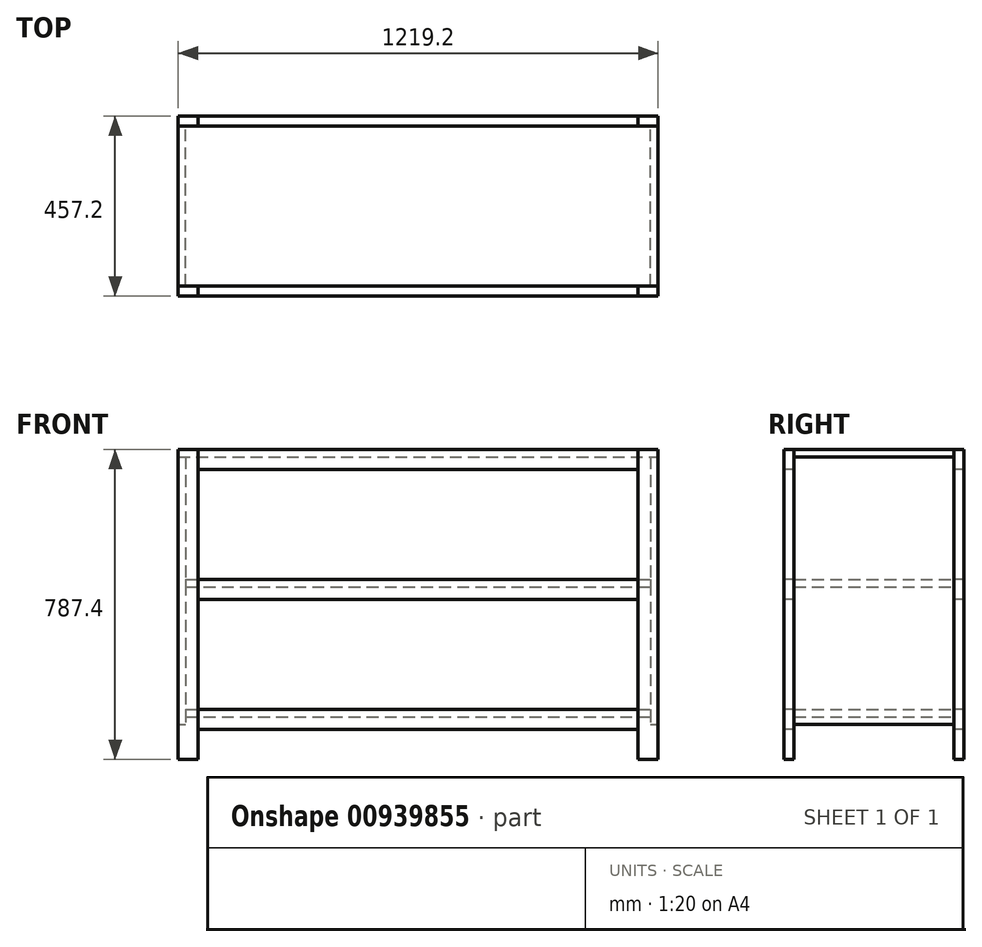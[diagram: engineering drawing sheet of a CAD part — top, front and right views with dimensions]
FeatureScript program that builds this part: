
annotation { "Feature Type Name" : "Feature", "Feature Type Description" : "" }
export const myFeature = defineFeature(function(context is Context, id is Id, definition is map)
    precondition{}
    {
        {
            var Q0;
            Q0=qCreatedBy(makeId("Front.planeOp"),FACE);
            var sketch = newSketch(context, id + "F0", { "sketchPlane" : qUnion([Q0])});
            skLineSegment(sketch, "E0", {"start": v(-1219.2, 0) * mm, "end": v(0, 0) * mm, "construction": true});
            skLineSegment(sketch, "E1", {"start": v(0, 787.4) * mm, "end": v(-1219.2, 787.4) * mm, "construction": true});
            skLineSegment(sketch, "E2", {"start": v(-1219.2, 787.4) * mm, "end": v(-1219.2, 0) * mm, "construction": true});
            skLineSegment(sketch, "E3", {"start": v(0, 0) * mm, "end": v(1219.2, 0) * mm, "construction": true});
            skLineSegment(sketch, "E4", {"start": v(1219.2, 0) * mm, "end": v(1219.2, 787.4) * mm, "construction": true});
            skLineSegment(sketch, "E5", {"start": v(1219.2, 787.4) * mm, "end": v(0, 787.4) * mm, "construction": true});
            skLineSegment(sketch, "E6", {"start": v(0, 787.4) * mm, "end": v(0, 0) * mm, "construction": true});
            skLineSegment(sketch, "E7.0", {"start": v(-19.05, 768.35) * mm, "end": v(-19.05, 88.9) * mm, "construction": true});
            skLineSegment(sketch, "E8.0", {"start": v(-1200.15, 768.35) * mm, "end": v(-1200.15, 88.9) * mm, "construction": true});
            skLineSegment(sketch, "E9.0", {"start": v(19.05, 787.4) * mm, "end": v(19.05, 0) * mm, "construction": true});
            skLineSegment(sketch, "E10.0", {"start": v(1200.15, 0) * mm, "end": v(1200.15, 787.4) * mm, "construction": true});
            skLineSegment(sketch, "E11.0", {"start": v(0, 768.35) * mm, "end": v(-1219.2, 768.35) * mm, "construction": true});
            skLineSegment(sketch, "E12.0", {"start": v(-19.05, 457.2) * mm, "end": v(-1200.15, 457.2) * mm, "construction": true});
            skLineSegment(sketch, "E13.0", {"start": v(-19.05, 438.15) * mm, "end": v(-1200.15, 438.15) * mm, "construction": true});
            skLineSegment(sketch, "E14.0", {"start": v(-19.05, 127) * mm, "end": v(-1200.15, 127) * mm, "construction": true});
            skLineSegment(sketch, "E15.0", {"start": v(-19.05, 107.95) * mm, "end": v(-1200.15, 107.95) * mm, "construction": true});
            skLineSegment(sketch, "E16.0", {"start": v(0, 88.9) * mm, "end": v(-19.05, 88.9) * mm, "construction": true});
            skLineSegment(sketch, "E17.trimOffspring", {"start": v(-1200.15, 88.9) * mm, "end": v(-1219.2, 88.9) * mm, "construction": true});
            skLineSegment(sketch, "E18.bottom", {"start": v(-1219.2, 787.4) * mm, "end": v(0, 787.4) * mm});
            skLineSegment(sketch, "E18.top", {"start": v(-1219.2, 768.35) * mm, "end": v(0, 768.35) * mm});
            skLineSegment(sketch, "E18.left", {"start": v(-1219.2, 787.4) * mm, "end": v(-1219.2, 768.35) * mm});
            skLineSegment(sketch, "E18.right", {"start": v(0, 787.4) * mm, "end": v(0, 768.35) * mm});
            skLineSegment(sketch, "E19.bottom", {"start": v(-1219.2, 768.35) * mm, "end": v(-1200.15, 768.35) * mm});
            skLineSegment(sketch, "E19.top", {"start": v(-1219.2, 88.9) * mm, "end": v(-1200.15, 88.9) * mm});
            skLineSegment(sketch, "E19.left", {"start": v(-1219.2, 768.35) * mm, "end": v(-1219.2, 88.9) * mm});
            skLineSegment(sketch, "E19.right", {"start": v(-1200.15, 768.35) * mm, "end": v(-1200.15, 88.9) * mm});
            skLineSegment(sketch, "E20.bottom", {"start": v(-19.05, 768.35) * mm, "end": v(0, 768.35) * mm});
            skLineSegment(sketch, "E20.top", {"start": v(-19.05, 88.9) * mm, "end": v(0, 88.9) * mm});
            skLineSegment(sketch, "E20.left", {"start": v(-19.05, 768.35) * mm, "end": v(-19.05, 88.9) * mm});
            skLineSegment(sketch, "E20.right", {"start": v(0, 768.35) * mm, "end": v(0, 88.9) * mm});
            skLineSegment(sketch, "E21.bottom", {"start": v(-1200.15, 457.2) * mm, "end": v(-19.05, 457.2) * mm});
            skLineSegment(sketch, "E21.top", {"start": v(-1200.15, 438.15) * mm, "end": v(-19.05, 438.15) * mm});
            skLineSegment(sketch, "E21.left", {"start": v(-1200.15, 457.2) * mm, "end": v(-1200.15, 438.15) * mm});
            skLineSegment(sketch, "E21.right", {"start": v(-19.05, 457.2) * mm, "end": v(-19.05, 438.15) * mm});
            skLineSegment(sketch, "E22.bottom", {"start": v(-1200.15, 127) * mm, "end": v(-19.05, 127) * mm});
            skLineSegment(sketch, "E22.top", {"start": v(-1200.15, 107.95) * mm, "end": v(-19.05, 107.95) * mm});
            skLineSegment(sketch, "E22.left", {"start": v(-1200.15, 127) * mm, "end": v(-1200.15, 107.95) * mm});
            skLineSegment(sketch, "E22.right", {"start": v(-19.05, 127) * mm, "end": v(-19.05, 107.95) * mm});
            skSolve(sketch);
        }
        {
            var Q0;
            Q0=makeQuery(id+"F0.imprint","IMPRINT",FACE,{"disambiguationData":[TD([[makeQuery(id+"F0.imprint","IMPRINT",EDGE,{"derivedFrom":sQuery(id+"F0.wireOp",EDGE,"E18.bottom")}),-1.0]])]});
            extrude(context, id + "F1", {"entities" : qUnion([Q0]), "depth" : 406.4 * mm, "offsetDistance" : 25.4 * mm});
        }
        {
            var Q0;
            {var subQ7=sQuery(id+"F0.wireOp",EDGE,"E20.top");Q0=makeQuery(id+"F0.imprint","IMPRINT",FACE,{"disambiguationData":[TD([[makeQuery(id+"F0.imprint","IMPRINT",EDGE,{"derivedFrom":subQ7}),1.0]])]});}
            extrude(context, id + "F2", {"entities" : qUnion([Q0]), "depth" : 406.4 * mm, "offsetDistance" : 25.4 * mm});
        }
        {
            var Q0;
            {var subQ3=sQuery(id+"F0.wireOp",EDGE,"E19.top");Q0=makeQuery(id+"F0.imprint","IMPRINT",FACE,{"disambiguationData":[TD([[makeQuery(id+"F0.imprint","IMPRINT",EDGE,{"derivedFrom":subQ3}),1.0]])]});}
            extrude(context, id + "F3", {"entities" : qUnion([Q0]), "depth" : 406.4 * mm, "offsetDistance" : 25.4 * mm});
        }
        {
            var Q0;
            {var subQ2=sQuery(id+"F0.wireOp",EDGE,"E21.bottom");Q0=makeQuery(id+"F0.imprint","IMPRINT",FACE,{"disambiguationData":[TD([[makeQuery(id+"F0.imprint","IMPRINT",EDGE,{"derivedFrom":subQ2}),-1.0]])]});}
            extrude(context, id + "F4", {"entities" : qUnion([Q0]), "depth" : 406.4 * mm, "offsetDistance" : 25.4 * mm});
        }
        {
            var Q0;
            {var subQ0=sQuery(id+"F0.wireOp",EDGE,"E22.bottom");Q0=makeQuery(id+"F0.imprint","IMPRINT",FACE,{"disambiguationData":[TD([[makeQuery(id+"F0.imprint","IMPRINT",EDGE,{"derivedFrom":subQ0}),-1.0]])]});}
            extrude(context, id + "F5", {"entities" : qUnion([Q0]), "depth" : 406.4 * mm, "offsetDistance" : 25.4 * mm});
        }
        {
            var Q0;
            Q0=makeQuery(id+"F1.opExtrude","SWEPT_FACE",FACE,{"disambiguationData":[OSD([sQuery(id+"F0.wireOp",EDGE,"E18.bottom")])]});
            var sketch = newSketch(context, id + "F6", { "sketchPlane" : qUnion([Q0])});
            skLineSegment(sketch, "E23.0", {"start": v(-1219.2, -431.8) * mm, "end": v(0, -431.8) * mm});
            skLineSegment(sketch, "E24.0", {"start": v(-1168.4, -406.4) * mm, "end": v(-1168.4, 0) * mm});
            skLineSegment(sketch, "E25.0", {"start": v(-50.8, -406.4) * mm, "end": v(-50.8, 0) * mm});
            skLineSegment(sketch, "E26.bottom", {"start": v(-50.8, -406.4) * mm, "end": v(0, -406.4) * mm});
            skLineSegment(sketch, "E26.top", {"start": v(-50.8, -431.8) * mm, "end": v(0, -431.8) * mm});
            skLineSegment(sketch, "E26.left", {"start": v(-50.8, -406.4) * mm, "end": v(-50.8, -431.8) * mm});
            skLineSegment(sketch, "E26.right", {"start": v(0, -406.4) * mm, "end": v(0, -431.8) * mm});
            skLineSegment(sketch, "E27.bottom", {"start": v(-1168.4, -406.4) * mm, "end": v(-1219.2, -406.4) * mm});
            skLineSegment(sketch, "E27.top", {"start": v(-1168.4, -431.8) * mm, "end": v(-1219.2, -431.8) * mm});
            skLineSegment(sketch, "E27.left", {"start": v(-1168.4, -406.4) * mm, "end": v(-1168.4, -431.8) * mm});
            skLineSegment(sketch, "E27.right", {"start": v(-1219.2, -406.4) * mm, "end": v(-1219.2, -431.8) * mm});
            skSolve(sketch);
        }
        {
            var Q0;
            Q0=makeQuery(id+"F6.imprint","IMPRINT",FACE,{"disambiguationData":[TD([[makeQuery(id+"F6.imprint","IMPRINT",EDGE,{"derivedFrom":sQuery(id+"F6.wireOp",EDGE,"E27.bottom")}),-1.0]])]});
            extrude(context, id + "F7", {"entities" : qUnion([Q0]), "oppositeDirection" : true, "depth" : 787.4 * mm, "offsetDistance" : 25.4 * mm});
        }
        {
            var Q0;
            Q0=makeQuery(id+"F6.imprint","IMPRINT",FACE,{"disambiguationData":[TD([[makeQuery(id+"F6.imprint","IMPRINT",EDGE,{"derivedFrom":sQuery(id+"F6.wireOp",EDGE,"E26.bottom")}),-1.0]])]});
            extrude(context, id + "F8", {"entities" : qUnion([Q0]), "oppositeDirection" : true, "depth" : 787.4 * mm, "offsetDistance" : 25.4 * mm});
        }
        {
            var Q0;
            {var subQ2=sQuery(id+"F6.wireOp",EDGE,"E26.left");Q0=makeQuery(id+"F6.imprint","IMPRINT",FACE,{"disambiguationData":[TD([[makeQuery(id+"F6.imprint","IMPRINT",EDGE,{"derivedFrom":subQ2}),-1.0]])]});}
            extrude(context, id + "F9", {"entities" : qUnion([Q0]), "oppositeDirection" : true, "depth" : 50.8 * mm, "offsetDistance" : 25.4 * mm});
        }
        {
            var Q0;
            Q0=makeQuery(id+"F9.opExtrude","SWEPT_BODY",BODY,{"disambiguationData":[OSD([sQuery(id+"F0.wireOp",EDGE,"E18.bottom"),sQuery(id+"F6.wireOp",EDGE,"E23.0"),sQuery(id+"F6.wireOp",EDGE,"E26.left"),sQuery(id+"F6.wireOp",EDGE,"E27.left")])]});
            transform(context, id + "F10", {"entities" : qUnion([Q0]), "transformType" : TransformType.COPY});
        }
        {
            var Q0;
            Q0=makeQuery(id+"F9.opExtrude","SWEPT_BODY",BODY,{"disambiguationData":[OSD([sQuery(id+"F0.wireOp",EDGE,"E18.bottom"),sQuery(id+"F6.wireOp",EDGE,"E23.0"),sQuery(id+"F6.wireOp",EDGE,"E26.left"),sQuery(id+"F6.wireOp",EDGE,"E27.left")])]});
            transform(context, id + "F11", {"entities" : qUnion([Q0]), "transformType" : TransformType.TRANSLATION_3D, "dx" : 0 * mm, "dy" : 0 * mm, "dz" : -330.2 * mm, "makeCopy" : false});
        }
        {
            var Q0;
            Q0=makeQuery(id+"F9.opExtrude","SWEPT_BODY",BODY,{"disambiguationData":[OSD([sQuery(id+"F0.wireOp",EDGE,"E18.bottom"),sQuery(id+"F6.wireOp",EDGE,"E23.0"),sQuery(id+"F6.wireOp",EDGE,"E26.left"),sQuery(id+"F6.wireOp",EDGE,"E27.left")])]});
            transform(context, id + "F12", {"entities" : qUnion([Q0]), "transformType" : TransformType.COPY});
        }
        {
            var Q0;
            Q0=makeQuery(id+"F9.opExtrude","SWEPT_BODY",BODY,{"disambiguationData":[OSD([sQuery(id+"F0.wireOp",EDGE,"E18.bottom"),sQuery(id+"F6.wireOp",EDGE,"E23.0"),sQuery(id+"F6.wireOp",EDGE,"E26.left"),sQuery(id+"F6.wireOp",EDGE,"E27.left")])]});
            transform(context, id + "F13", {"entities" : qUnion([Q0]), "transformType" : TransformType.TRANSLATION_3D, "dx" : 0 * mm, "dy" : 0 * mm, "dz" : -330.2 * mm, "makeCopy" : false});
        }
        {
            var Q0;
            Q0=makeQuery(id+"F7.opExtrude","SWEPT_BODY",BODY,{"disambiguationData":[OSD([sQuery(id+"F6.wireOp",EDGE,"E23.0"),sQuery(id+"F6.wireOp",EDGE,"E27.bottom"),sQuery(id+"F6.wireOp",EDGE,"E27.left"),sQuery(id+"F6.wireOp",EDGE,"E27.right")])]});
            var Q1;
            Q1=makeQuery(id+"F10.opPattern","COPY",BODY,{"derivedFrom":makeQuery(id+"F9.opExtrude","SWEPT_BODY",BODY,{"disambiguationData":[OSD([sQuery(id+"F0.wireOp",EDGE,"E18.bottom"),sQuery(id+"F6.wireOp",EDGE,"E23.0"),sQuery(id+"F6.wireOp",EDGE,"E26.left"),sQuery(id+"F6.wireOp",EDGE,"E27.left")])]}),"instanceName":"1"});
            var Q2;
            Q2=makeQuery(id+"F12.opPattern","COPY",BODY,{"derivedFrom":makeQuery(id+"F9.opExtrude","SWEPT_BODY",BODY,{"disambiguationData":[OSD([sQuery(id+"F0.wireOp",EDGE,"E18.bottom"),sQuery(id+"F6.wireOp",EDGE,"E23.0"),sQuery(id+"F6.wireOp",EDGE,"E26.left"),sQuery(id+"F6.wireOp",EDGE,"E27.left")])]}),"instanceName":"1"});
            var Q3;
            Q3=makeQuery(id+"F9.opExtrude","SWEPT_BODY",BODY,{"disambiguationData":[OSD([sQuery(id+"F0.wireOp",EDGE,"E18.bottom"),sQuery(id+"F6.wireOp",EDGE,"E23.0"),sQuery(id+"F6.wireOp",EDGE,"E26.left"),sQuery(id+"F6.wireOp",EDGE,"E27.left")])]});
            var Q4;
            Q4=makeQuery(id+"F8.opExtrude","SWEPT_BODY",BODY,{"disambiguationData":[OSD([sQuery(id+"F6.wireOp",EDGE,"E23.0"),sQuery(id+"F6.wireOp",EDGE,"E26.bottom"),sQuery(id+"F6.wireOp",EDGE,"E26.left"),sQuery(id+"F6.wireOp",EDGE,"E26.right")])]});
            transform(context, id + "F14", {"entities" : qUnion([Q0, Q1, Q2, Q3, Q4]), "transformType" : TransformType.COPY});
        }
        {
            var Q0;
            Q0=makeQuery(id+"F14.opPattern","COPY",BODY,{"derivedFrom":makeQuery(id+"F8.opExtrude","SWEPT_BODY",BODY,{"disambiguationData":[OSD([sQuery(id+"F6.wireOp",EDGE,"E23.0"),sQuery(id+"F6.wireOp",EDGE,"E26.bottom"),sQuery(id+"F6.wireOp",EDGE,"E26.left"),sQuery(id+"F6.wireOp",EDGE,"E26.right")])]}),"instanceName":"1"});
            var Q1;
            Q1=makeQuery(id+"F14.opPattern","COPY",BODY,{"derivedFrom":makeQuery(id+"F9.opExtrude","SWEPT_BODY",BODY,{"disambiguationData":[OSD([sQuery(id+"F0.wireOp",EDGE,"E18.bottom"),sQuery(id+"F6.wireOp",EDGE,"E23.0"),sQuery(id+"F6.wireOp",EDGE,"E26.left"),sQuery(id+"F6.wireOp",EDGE,"E27.left")])]}),"instanceName":"1"});
            var Q2;
            Q2=makeQuery(id+"F14.opPattern","COPY",BODY,{"derivedFrom":makeQuery(id+"F10.opPattern","COPY",BODY,{"derivedFrom":makeQuery(id+"F9.opExtrude","SWEPT_BODY",BODY,{"disambiguationData":[OSD([sQuery(id+"F0.wireOp",EDGE,"E18.bottom"),sQuery(id+"F6.wireOp",EDGE,"E23.0"),sQuery(id+"F6.wireOp",EDGE,"E26.left"),sQuery(id+"F6.wireOp",EDGE,"E27.left")])]}),"instanceName":"1"}),"instanceName":"1"});
            var Q3;
            Q3=makeQuery(id+"F14.opPattern","COPY",BODY,{"derivedFrom":makeQuery(id+"F12.opPattern","COPY",BODY,{"derivedFrom":makeQuery(id+"F9.opExtrude","SWEPT_BODY",BODY,{"disambiguationData":[OSD([sQuery(id+"F0.wireOp",EDGE,"E18.bottom"),sQuery(id+"F6.wireOp",EDGE,"E23.0"),sQuery(id+"F6.wireOp",EDGE,"E26.left"),sQuery(id+"F6.wireOp",EDGE,"E27.left")])]}),"instanceName":"1"}),"instanceName":"1"});
            var Q4;
            Q4=makeQuery(id+"F14.opPattern","COPY",BODY,{"derivedFrom":makeQuery(id+"F7.opExtrude","SWEPT_BODY",BODY,{"disambiguationData":[OSD([sQuery(id+"F6.wireOp",EDGE,"E23.0"),sQuery(id+"F6.wireOp",EDGE,"E27.bottom"),sQuery(id+"F6.wireOp",EDGE,"E27.left"),sQuery(id+"F6.wireOp",EDGE,"E27.right")])]}),"instanceName":"1"});
            transform(context, id + "F15", {"entities" : qUnion([Q0, Q1, Q2, Q3, Q4]), "transformType" : TransformType.TRANSLATION_3D, "dx" : 0 * mm, "dy" : 431.8 * mm, "dz" : 0 * mm, "makeCopy" : false});
        }
    });
